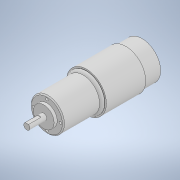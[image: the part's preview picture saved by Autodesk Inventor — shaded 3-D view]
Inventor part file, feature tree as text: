
AUTODESK INVENTOR PART (.ipt)
format: ipt  version: 2021 (Build 250183000, 183)  size: 173,568 bytes
history: native  units: mm
features: extrude x9, sketch x9, other x1, fillet x1, chamfer x1
ambient origin geometry x8: Origin, YZ Plane, XZ Plane, XY Plane, X Axis, Y Axis, Z Axis, Center Point
bodies: Body1 (feature_tree)
feature tree (21):
  other  "ソリッド1"
  extrude  "押し出し1"  Depth=35.8mm
  fillet  "フィレット1"  Radius=3.3mm
  extrude  "押し出し2"  Depth=3.0mm
  extrude  "押し出し3"  Depth=38.5mm
  extrude  "押し出し4"  Depth=38.0mm TaperAngle=0.0deg
  extrude  "押し出し5"  Depth=35.8mm
  chamfer  "面取り1"  Distance=15.7mm
  extrude  "押し出し6"  Depth=3.17mm
  extrude  "押し出し7"  Depth=10.7mm TaperAngle=0.0deg
  extrude  "押し出し8"  Depth=32.0mm
  extrude  "押し出し9"  Depth=34.9mm TaperAngle=0.0deg
  sketch  "スケッチ1"
  sketch  "スケッチ2"
  sketch  "スケッチ3"
  sketch  "スケッチ4"
  sketch  "スケッチ5"
  sketch  "スケッチ6"
  sketch  "スケッチ7"
  sketch  "スケッチ8"
  sketch  "スケッチ9"
